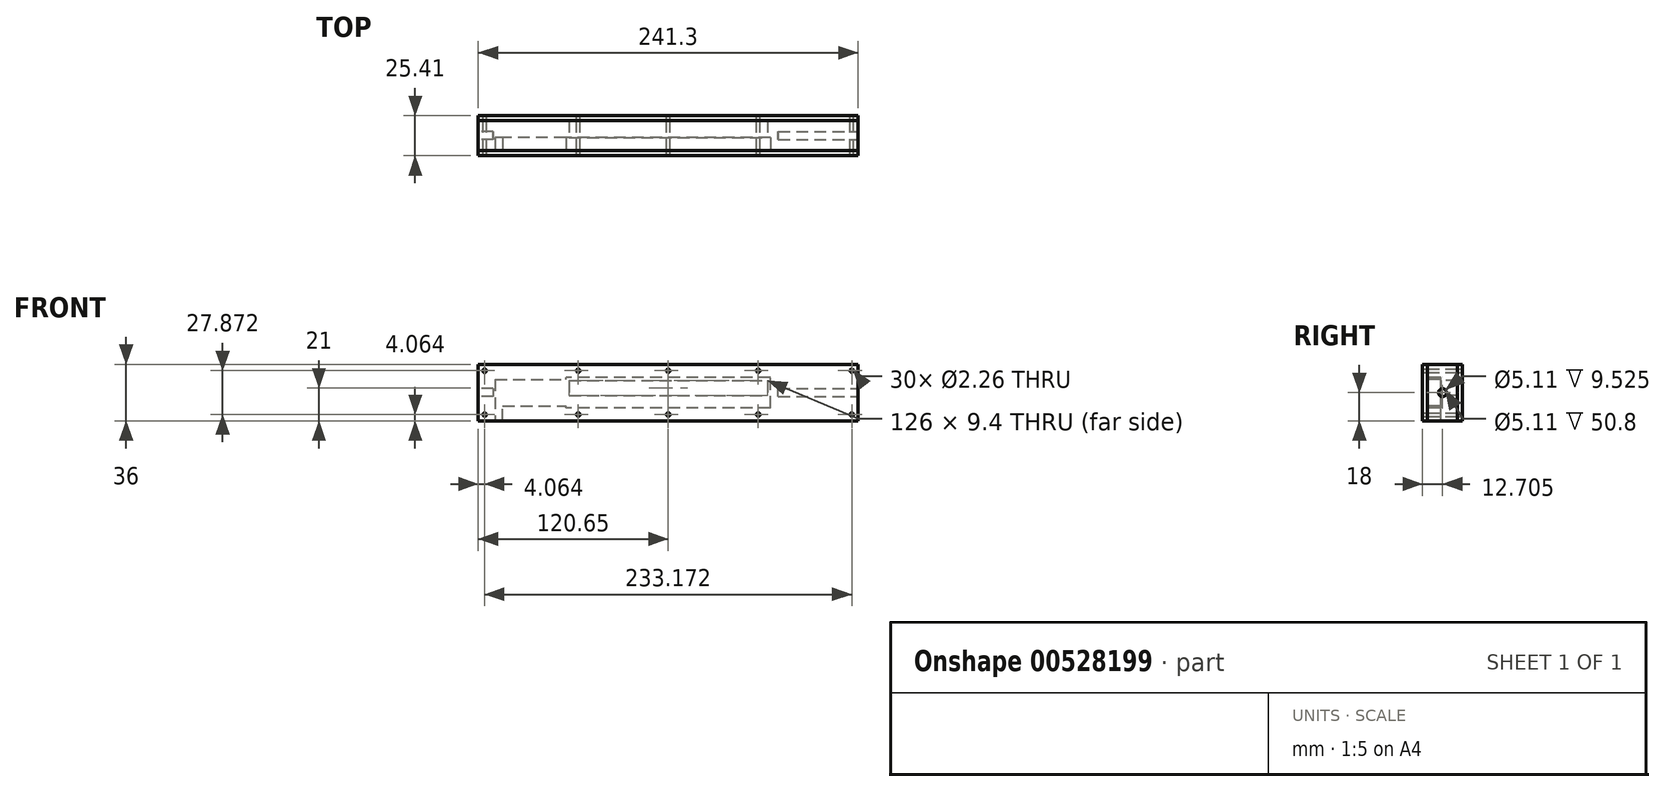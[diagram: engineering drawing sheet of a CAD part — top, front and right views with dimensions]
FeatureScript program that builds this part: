
annotation { "Feature Type Name" : "Feature", "Feature Type Description" : "" }
export const myFeature = defineFeature(function(context is Context, id is Id, definition is map)
    precondition{}
    {
        {
            var Q0;
            Q0=qCreatedBy(makeId("Front.planeOp"),FACE);
            var sketch = newSketch(context, id + "F0", { "sketchPlane" : qUnion([Q0])});
            skLineSegment(sketch, "E0.bottom", {"start": v(0, 0) * mm, "end": v(241.3, 0) * mm});
            skLineSegment(sketch, "E0.top", {"start": v(0, 36) * mm, "end": v(241.3, 36) * mm});
            skLineSegment(sketch, "E0.left", {"start": v(0, 0) * mm, "end": v(0, 36) * mm});
            skLineSegment(sketch, "E0.right", {"start": v(241.3, 0) * mm, "end": v(241.3, 36) * mm});
            skSolve(sketch);
        }
        {
            var Q0;
            Q0 = qSketchRegion(id + "F0", true);
            extrude(context, id + "F1", {"entities" : qUnion([Q0]), "depth" : 19.05 * mm, "offsetDistance" : 25.4 * mm});
        }
        {
            var Q0;
            Q0=makeQuery(id+"F1.opExtrude","CAP_FACE",FACE,{"disambiguationData":[OSD([sQuery(id+"F0.wireOp",EDGE,"E0.bottom"),sQuery(id+"F0.wireOp",EDGE,"E0.top"),sQuery(id+"F0.wireOp",EDGE,"E0.left"),sQuery(id+"F0.wireOp",EDGE,"E0.right")])],"isStart":false});
            var sketch = newSketch(context, id + "F2", { "sketchPlane" : qUnion([Q0])});
            skLineSegment(sketch, "E1", {"start": v(120.65, 36) * mm, "end": v(120.65, -53.1) * mm, "construction": true});
            skLineSegment(sketch, "E2", {"start": v(0, 18) * mm, "end": v(282.53, 18) * mm, "construction": true});
            skLineSegment(sketch, "E3.bottom", {"start": v(185.65, 8.3) * mm, "end": v(55.65, 8.3) * mm});
            skLineSegment(sketch, "E3.top", {"start": v(185.65, 27.7) * mm, "end": v(55.65, 27.7) * mm});
            skLineSegment(sketch, "E3.left", {"start": v(185.65, 8.3) * mm, "end": v(185.65, 27.7) * mm});
            skLineSegment(sketch, "E3.right", {"start": v(55.65, 8.3) * mm, "end": v(55.65, 27.7) * mm});
            skPoint(sketch, "E3.middle", {"position": v(120.65, 18) * mm});
            skSolve(sketch);
        }
        {
            var Q0;
            Q0 = qSketchRegion(id + "F2", true);
            extrude(context, id + "F3", {"entities" : qUnion([Q0]), "operationType" : NewBodyOperationType.REMOVE, "oppositeDirection" : true, "depth" : 8.5 * mm, "offsetDistance" : 25.4 * mm});
        }
        {
            var Q0;
            Q0=makeQuery(id+"F3.boolean.opBoolean","COPY",FACE,{"derivedFrom":makeQuery(id+"F3.opExtrude","CAP_FACE",FACE,{"disambiguationData":[OSD([sQuery(id+"F2.wireOp",EDGE,"E3.bottom"),sQuery(id+"F2.wireOp",EDGE,"E3.top"),sQuery(id+"F2.wireOp",EDGE,"E3.left"),sQuery(id+"F2.wireOp",EDGE,"E3.right")])],"isStart":false})});
            var sketch = newSketch(context, id + "F4", { "sketchPlane" : qUnion([Q0])});
            skLineSegment(sketch, "E4.bottom", {"start": v(57.65, 25.7) * mm, "end": v(183.65, 25.7) * mm});
            skLineSegment(sketch, "E4.top", {"start": v(57.65, 16.3) * mm, "end": v(183.65, 16.3) * mm});
            skLineSegment(sketch, "E4.left", {"start": v(57.65, 25.7) * mm, "end": v(57.65, 16.3) * mm});
            skLineSegment(sketch, "E4.right", {"start": v(183.65, 25.7) * mm, "end": v(183.65, 16.3) * mm});
            skSolve(sketch);
        }
        {
            var Q0;
            Q0 = qSketchRegion(id + "F4", true);
            extrude(context, id + "F5", {"entities" : qUnion([Q0]), "operationType" : NewBodyOperationType.REMOVE, "endBound" : BoundingType.THROUGH_ALL, "oppositeDirection" : true, "depth" : 25.4 * mm, "offsetDistance" : 25.4 * mm});
        }
        {
            var Q0;
            Q0=makeQuery(id+"F1.opExtrude","CAP_FACE",FACE,{"disambiguationData":[OSD([sQuery(id+"F0.wireOp",EDGE,"E0.bottom"),sQuery(id+"F0.wireOp",EDGE,"E0.top"),sQuery(id+"F0.wireOp",EDGE,"E0.left"),sQuery(id+"F0.wireOp",EDGE,"E0.right")])],"isStart":false});
            var sketch = newSketch(context, id + "F6", { "sketchPlane" : qUnion([Q0])});
            skLineSegment(sketch, "E5.bottom", {"start": v(10.65, 26.5) * mm, "end": v(55.65, 26.5) * mm});
            skLineSegment(sketch, "E5.top", {"start": v(10.65, 9.5) * mm, "end": v(55.65, 9.5) * mm});
            skLineSegment(sketch, "E5.left", {"start": v(10.65, 26.5) * mm, "end": v(10.65, 9.5) * mm});
            skLineSegment(sketch, "E5.right", {"start": v(55.65, 26.5) * mm, "end": v(55.65, 9.5) * mm});
            skPoint(sketch, "E6", {"position": v(55.65, 18) * mm});
            skSolve(sketch);
        }
        {
            var Q0;
            Q0 = qSketchRegion(id + "F6", true);
            var Q1;
            Q1=makeQuery(id+"F3.boolean.opBoolean","COPY",FACE,{"derivedFrom":makeQuery(id+"F3.opExtrude","CAP_FACE",FACE,{"disambiguationData":[OSD([sQuery(id+"F2.wireOp",EDGE,"E3.bottom"),sQuery(id+"F2.wireOp",EDGE,"E3.top"),sQuery(id+"F2.wireOp",EDGE,"E3.left"),sQuery(id+"F2.wireOp",EDGE,"E3.right")])],"isStart":false})});
            extrude(context, id + "F7", {"entities" : qUnion([Q0]), "operationType" : NewBodyOperationType.REMOVE, "endBound" : BoundingType.UP_TO_SURFACE, "oppositeDirection" : true, "depth" : 25.4 * mm, "endBoundEntityFace" : qUnion([Q1]), "offsetDistance" : 25.4 * mm});
        }
        {
            var Q0;
            Q0=makeQuery(id+"F1.opExtrude","SWEPT_FACE",FACE,{"disambiguationData":[OSD([sQuery(id+"F0.wireOp",EDGE,"E0.left")])]});
            var sketch = newSketch(context, id + "F8", { "sketchPlane" : qUnion([Q0])});
            skCircle(sketch, "E7", {"center": v(9.53, 18) * mm, "radius": 2.55 * mm});
            skLineSegment(sketch, "E8", {"start": v(9.53, 36) * mm, "end": v(9.53, 8.52) * mm, "construction": true});
            skLineSegment(sketch, "E9", {"start": v(0, 18) * mm, "end": v(23.51, 18) * mm, "construction": true});
            skSolve(sketch);
        }
        {
            var Q0;
            Q0 = qSketchRegion(id + "F8", true);
            extrude(context, id + "F9", {"entities" : qUnion([Q0]), "operationType" : NewBodyOperationType.REMOVE, "oppositeDirection" : true, "depth" : 9.52 * mm, "offsetDistance" : 25.4 * mm});
        }
        {
            var Q0;
            Q0=makeQuery(id+"F1.opExtrude","SWEPT_FACE",FACE,{"disambiguationData":[OSD([sQuery(id+"F0.wireOp",EDGE,"E0.right")])]});
            var sketch = newSketch(context, id + "F10", { "sketchPlane" : qUnion([Q0])});
            skCircle(sketch, "E10.0", {"center": v(-9.53, 18) * mm, "radius": 2.55 * mm});
            skLineSegment(sketch, "E10.1", {"start": v(-9.53, 36) * mm, "end": v(-9.53, 8.52) * mm, "construction": true});
            skLineSegment(sketch, "E10.2", {"start": v(0, 18) * mm, "end": v(-23.51, 18) * mm, "construction": true});
            skSolve(sketch);
        }
        {
            var Q0;
            Q0 = qSketchRegion(id + "F10", true);
            extrude(context, id + "F11", {"entities" : qUnion([Q0]), "operationType" : NewBodyOperationType.REMOVE, "oppositeDirection" : true, "depth" : 50.8 * mm, "offsetDistance" : 25.4 * mm});
        }
        {
            var Q0;
            Q0=makeQuery(id+"F7.boolean.opBoolean","COPY",FACE,{"derivedFrom":makeQuery(id+"F7.opExtrude","SWEPT_FACE",FACE,{"disambiguationData":[OSD([sQuery(id+"F6.wireOp",EDGE,"E5.top")])]})});
            var sketch = newSketch(context, id + "F12", { "sketchPlane" : qUnion([Q0])});
            skLineSegment(sketch, "E11.bottom", {"start": v(10.65, -10.55) * mm, "end": v(15.41, -10.55) * mm});
            skLineSegment(sketch, "E11.top", {"start": v(10.65, -19.05) * mm, "end": v(15.41, -19.05) * mm});
            skLineSegment(sketch, "E11.left", {"start": v(10.65, -10.55) * mm, "end": v(10.65, -19.05) * mm});
            skLineSegment(sketch, "E11.right", {"start": v(15.41, -10.55) * mm, "end": v(15.41, -19.05) * mm});
            skSolve(sketch);
        }
        {
            var Q0;
            Q0 = qSketchRegion(id + "F12", true);
            extrude(context, id + "F13", {"entities" : qUnion([Q0]), "operationType" : NewBodyOperationType.REMOVE, "endBound" : BoundingType.THROUGH_ALL, "oppositeDirection" : true, "depth" : 25.4 * mm, "offsetDistance" : 25.4 * mm});
        }
        {
            var Q0;
            Q0=makeQuery(id+"F1.opExtrude","CAP_FACE",FACE,{"disambiguationData":[OSD([sQuery(id+"F0.wireOp",EDGE,"E0.bottom"),sQuery(id+"F0.wireOp",EDGE,"E0.top"),sQuery(id+"F0.wireOp",EDGE,"E0.left"),sQuery(id+"F0.wireOp",EDGE,"E0.right")])],"isStart":true});
            var sketch = newSketch(context, id + "F14", { "sketchPlane" : qUnion([Q0])});
            skLineSegment(sketch, "E12.0", {"start": v(0, 36) * mm, "end": v(-241.3, 36) * mm});
            skLineSegment(sketch, "E13.0", {"start": v(-241.3, 0) * mm, "end": v(-241.3, 36) * mm});
            skLineSegment(sketch, "E14.0", {"start": v(0, 0) * mm, "end": v(-241.3, 0) * mm});
            skLineSegment(sketch, "E15.0", {"start": v(0, 0) * mm, "end": v(0, 36) * mm});
            skSolve(sketch);
        }
        {
            var Q0;
            Q0 = qSketchRegion(id + "F14", true);
            extrude(context, id + "F15", {"entities" : qUnion([Q0]), "depth" : 3.17 * mm, "offsetDistance" : 25.4 * mm});
        }
        {
            var Q0;
            Q0=makeQuery(id+"F15.opExtrude","CAP_FACE",FACE,{"disambiguationData":[OSD([sQuery(id+"F14.wireOp",EDGE,"E12.0"),sQuery(id+"F14.wireOp",EDGE,"E13.0"),sQuery(id+"F14.wireOp",EDGE,"E14.0"),sQuery(id+"F14.wireOp",EDGE,"E15.0")])],"isStart":false});
            var sketch = newSketch(context, id + "F16", { "sketchPlane" : qUnion([Q0])});
            skLineSegment(sketch, "E16.0", {"start": v(-4.06, 31.94) * mm, "end": v(-237.24, 31.94) * mm, "construction": true});
            skLineSegment(sketch, "E16.1", {"start": v(-4.06, 4.06) * mm, "end": v(-4.06, 31.94) * mm, "construction": true});
            skLineSegment(sketch, "E16.2", {"start": v(-4.06, 4.06) * mm, "end": v(-237.24, 4.06) * mm, "construction": true});
            skLineSegment(sketch, "E16.3", {"start": v(-237.24, 4.06) * mm, "end": v(-237.24, 31.94) * mm, "construction": true});
            skLineSegment(sketch, "E17.0", {"start": v(6.35, 42.35) * mm, "end": v(-247.65, 42.35) * mm});
            skLineSegment(sketch, "E17.1", {"start": v(6.35, -6.35) * mm, "end": v(6.35, 42.35) * mm});
            skLineSegment(sketch, "E17.2", {"start": v(-247.65, -6.35) * mm, "end": v(6.35, -6.35) * mm});
            skLineSegment(sketch, "E17.3", {"start": v(-247.65, 42.35) * mm, "end": v(-247.65, -6.35) * mm});
            skLineSegment(sketch, "E18", {"start": v(-120.65, 0) * mm, "end": v(-120.65, 36) * mm, "construction": true});
            skLineSegment(sketch, "E19", {"start": v(-177.8, 48.7) * mm, "end": v(-177.8, -22) * mm, "construction": true});
            skLineSegment(sketch, "E20", {"start": v(-63.5, 52.24) * mm, "end": v(-63.5, -27.03) * mm, "construction": true});
            skPoint(sketch, "E21", {"position": v(-177.8, 31.94) * mm});
            skPoint(sketch, "E22", {"position": v(-120.65, 31.94) * mm});
            skPoint(sketch, "E23", {"position": v(-120.65, 4.06) * mm});
            skPoint(sketch, "E24", {"position": v(-63.5, 31.94) * mm});
            skPoint(sketch, "E25", {"position": v(-63.5, 4.06) * mm});
            skPoint(sketch, "E26", {"position": v(-177.8, 4.06) * mm});
            skSolve(sketch);
        }
        {
            var Q0;
            Q0=makeQuery(id+"F1.opExtrude","CAP_FACE",FACE,{"disambiguationData":[OSD([sQuery(id+"F0.wireOp",EDGE,"E0.bottom"),sQuery(id+"F0.wireOp",EDGE,"E0.top"),sQuery(id+"F0.wireOp",EDGE,"E0.left"),sQuery(id+"F0.wireOp",EDGE,"E0.right")])],"isStart":false});
            var sketch = newSketch(context, id + "F17", { "sketchPlane" : qUnion([Q0])});
            skLineSegment(sketch, "E27.0", {"start": v(0, 36) * mm, "end": v(241.3, 36) * mm});
            skLineSegment(sketch, "E28.0", {"start": v(241.3, 0) * mm, "end": v(241.3, 36) * mm});
            skLineSegment(sketch, "E29.0", {"start": v(0, 0) * mm, "end": v(241.3, 0) * mm});
            skLineSegment(sketch, "E30.0", {"start": v(0, 0) * mm, "end": v(0, 36) * mm});
            skSolve(sketch);
        }
        {
            var Q0;
            Q0 = qSketchRegion(id + "F17", true);
            extrude(context, id + "F18", {"entities" : qUnion([Q0]), "depth" : 3.17 * mm, "offsetDistance" : 25.4 * mm});
        }
        {
            var Q0;
            Q0=sQuery(id+"F16.wireOp",VERTEX,"E21");
            var Q1;
            Q1=sQuery(id+"F16.wireOp",VERTEX,"E22");
            var Q2;
            Q2=sQuery(id+"F16.wireOp",VERTEX,"E26");
            var Q3;
            Q3=sQuery(id+"F16.wireOp",VERTEX,"E23");
            var Q4;
            Q4=sQuery(id+"F16.wireOp",VERTEX,"E24");
            var Q5;
            Q5=sQuery(id+"F16.wireOp",VERTEX,"E25");
            var Q6;
            Q6=sQuery(id+"F16.wireOp",VERTEX,"E16.3.start");
            var Q7;
            Q7=sQuery(id+"F16.wireOp",VERTEX,"E16.3.end");
            var Q8;
            Q8=sQuery(id+"F16.wireOp",VERTEX,"E16.1.end");
            var Q9;
            Q9=sQuery(id+"F16.wireOp",VERTEX,"E16.1.start");
            var Q10;
            Q10=makeQuery(id+"F15.opExtrude","SWEPT_BODY",BODY,{"disambiguationData":[OSD([sQuery(id+"F14.wireOp",EDGE,"E12.0"),sQuery(id+"F14.wireOp",EDGE,"E13.0"),sQuery(id+"F14.wireOp",EDGE,"E14.0"),sQuery(id+"F14.wireOp",EDGE,"E15.0")])]});
            var Q11;
            Q11=makeQuery(id+"F1.opExtrude","SWEPT_BODY",BODY,{"disambiguationData":[OSD([sQuery(id+"F0.wireOp",EDGE,"E0.bottom"),sQuery(id+"F0.wireOp",EDGE,"E0.top"),sQuery(id+"F0.wireOp",EDGE,"E0.left"),sQuery(id+"F0.wireOp",EDGE,"E0.right")])]});
            var Q12;
            Q12=makeQuery(id+"F18.opExtrude","SWEPT_BODY",BODY,{"disambiguationData":[OSD([sQuery(id+"F17.wireOp",EDGE,"E27.0"),sQuery(id+"F17.wireOp",EDGE,"E28.0"),sQuery(id+"F17.wireOp",EDGE,"E29.0"),sQuery(id+"F17.wireOp",EDGE,"E30.0")])]});
            hole(context, id + "F19", {"style" : HoleStyle.SIMPLE, "endStyle" : HoleEndStyle.THROUGH, "standardTappedOrClearance" : lookupTablePath({ "standard" : "ANSI", "engagement" : "75%", "pitch" : "40 tpi", "size" : "#4", "type" : "Tapped" }), "standardBlindInLast" : lookupTablePath({ "standard" : "ANSI", "engagement" : "75%", "pitch" : "40 tpi", "size" : "#4", "type" : "Tapped" }), "holeDiameter" : 2.26 * mm, "majorDiameter" : 2.84 * mm, "showTappedDepth" : true, "isTappedThrough" : true, "tappedDepth" : 12.7 * mm, "tapClearance" : 3, "startFromSketch" : true, "locations" : qUnion([Q0, Q1, Q2, Q3, Q4, Q5, Q6, Q7, Q8, Q9]), "scope" : qUnion([Q10, Q11, Q12])});
        }
    });
